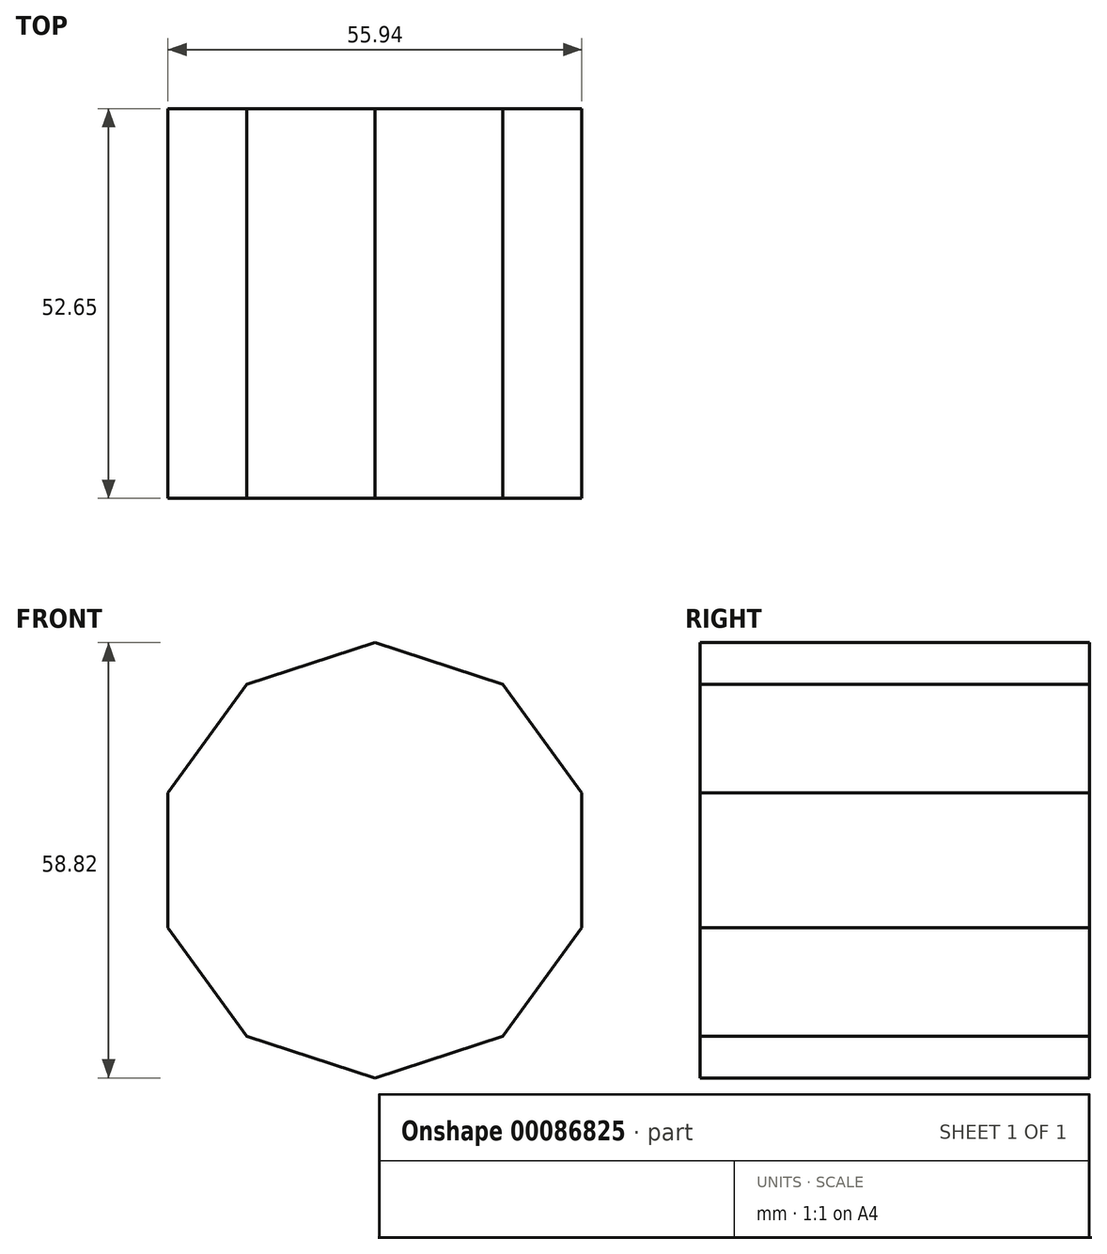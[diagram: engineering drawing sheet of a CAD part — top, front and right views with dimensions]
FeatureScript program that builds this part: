
annotation { "Feature Type Name" : "Feature", "Feature Type Description" : "" }
export const myFeature = defineFeature(function(context is Context, id is Id, definition is map)
    precondition{}
    {
        {
            var Q0;
            Q0=qCreatedBy(makeId("Front.planeOp"),FACE);
            var sketch = newSketch(context, id + "F0", { "sketchPlane" : qUnion([Q0])});
            skCircle(sketch, "E0.cCircle", {"center": v(0, 0) * mm, "radius": 27.97 * mm, "construction": true});
            skLineSegment(sketch, "E0.0", {"start": v(27.97, 9.09) * mm, "end": v(27.97, -9.09) * mm});
            skLineSegment(sketch, "E0.1", {"start": v(27.97, -9.09) * mm, "end": v(17.29, -23.8) * mm});
            skLineSegment(sketch, "E0.2", {"start": v(17.29, -23.8) * mm, "end": v(0, -29.41) * mm});
            skLineSegment(sketch, "E0.3", {"start": v(0, -29.41) * mm, "end": v(-17.29, -23.8) * mm});
            skLineSegment(sketch, "E0.4", {"start": v(-17.29, -23.8) * mm, "end": v(-27.97, -9.09) * mm});
            skLineSegment(sketch, "E0.5", {"start": v(-27.97, -9.09) * mm, "end": v(-27.97, 9.09) * mm});
            skLineSegment(sketch, "E0.6", {"start": v(-27.97, 9.09) * mm, "end": v(-17.29, 23.8) * mm});
            skLineSegment(sketch, "E0.7", {"start": v(-17.29, 23.8) * mm, "end": v(0, 29.41) * mm});
            skLineSegment(sketch, "E0.8", {"start": v(0, 29.41) * mm, "end": v(17.29, 23.8) * mm});
            skLineSegment(sketch, "E0.9", {"start": v(17.29, 23.8) * mm, "end": v(27.97, 9.09) * mm});
            skPoint(sketch, "E0.0.midPoint", {"position": v(27.97, 0) * mm});
            skSolve(sketch);
        }
        {
            var Q0;
            Q0=makeQuery(id+"F0.imprint","IMPRINT",FACE,{"disambiguationData":[TD([[makeQuery(id+"F0.imprint","IMPRINT",EDGE,{"derivedFrom":sQuery(id+"F0.wireOp",EDGE,"E0.0")}),-1.0]])]});
            extrude(context, id + "F1", {"entities" : qUnion([Q0]), "depth" : 52.65 * mm});
        }
    });
